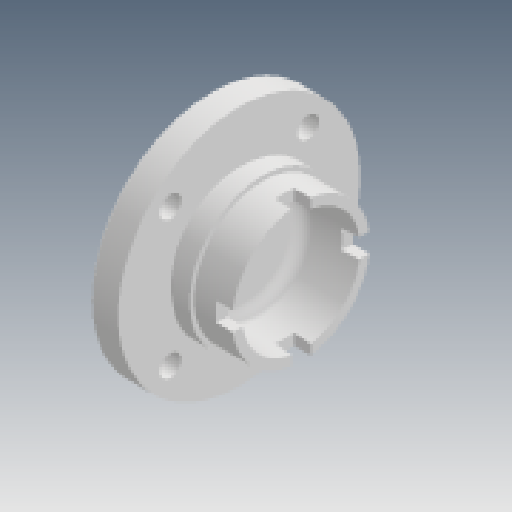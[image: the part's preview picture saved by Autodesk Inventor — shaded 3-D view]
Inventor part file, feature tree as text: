
AUTODESK INVENTOR PART (.ipt)
format: ipt  version: 2025 (Build 290162000, 162)  size: 406,016 bytes
history: native  units: in
note: dims shown in document units (in); Inventor stores cm internally (conversion verified against a paired STEP export)
features: sketch x5, extrude x3, revolve x1, chamfer x1, fillet x1
ambient origin geometry x8: Origin, YZ Plane, XZ Plane, XY Plane, X Axis, Y Axis, Z Axis, Center Point
bodies: 实体1 (feature_tree)
feature tree (11):
  revolve  "旋转1"  [1 undecoded]
  extrude  "拉伸1"  Depth=0.4724in
  extrude  "拉伸2"  Depth=1.1417in
  extrude  "拉伸3"  Depth=0.3937in
  chamfer  "倒角1"  Angle=45.0deg  [1 undecoded]
  fillet  "圆角1"  Radius=0.0394in
  sketch  "草图1"  dims[d3=0.315in d0=0.3543in d1=1.0236in d2=2.0079in]
  sketch  "草图2"  dims[d6=1.2205in d7=1.1417in]
  sketch  "草图3"  dims[d8=0.3937in d9=0.0984in]
  sketch  "草图4"  dims[d10=1.1417in d11=45.0deg d12=0.0394in d13=0.5906in d14=0.9843in d15=0.5792in d16=90.0deg d17=0.2756in d18=0.315in d19=0.0in d20=0.2756in d21=0.315in d22=0.0in d23=0.3543in d24=1.6142in d25=1.5748in d27=360.0deg d29=0.315in d30=0.0in d31=0.0394in d32=0.0787in d33=45.0deg d34=0.1969in d35=45.0deg]
  sketch  "草图 - 环形阵列1"  dims[d4=1.0236in d5=0.4724in]
note: 2 required parameter values undecoded (feature->parameter linkage not recoverable at this tier; creation-order binding heuristic only, values carry confidence <= 0.55)